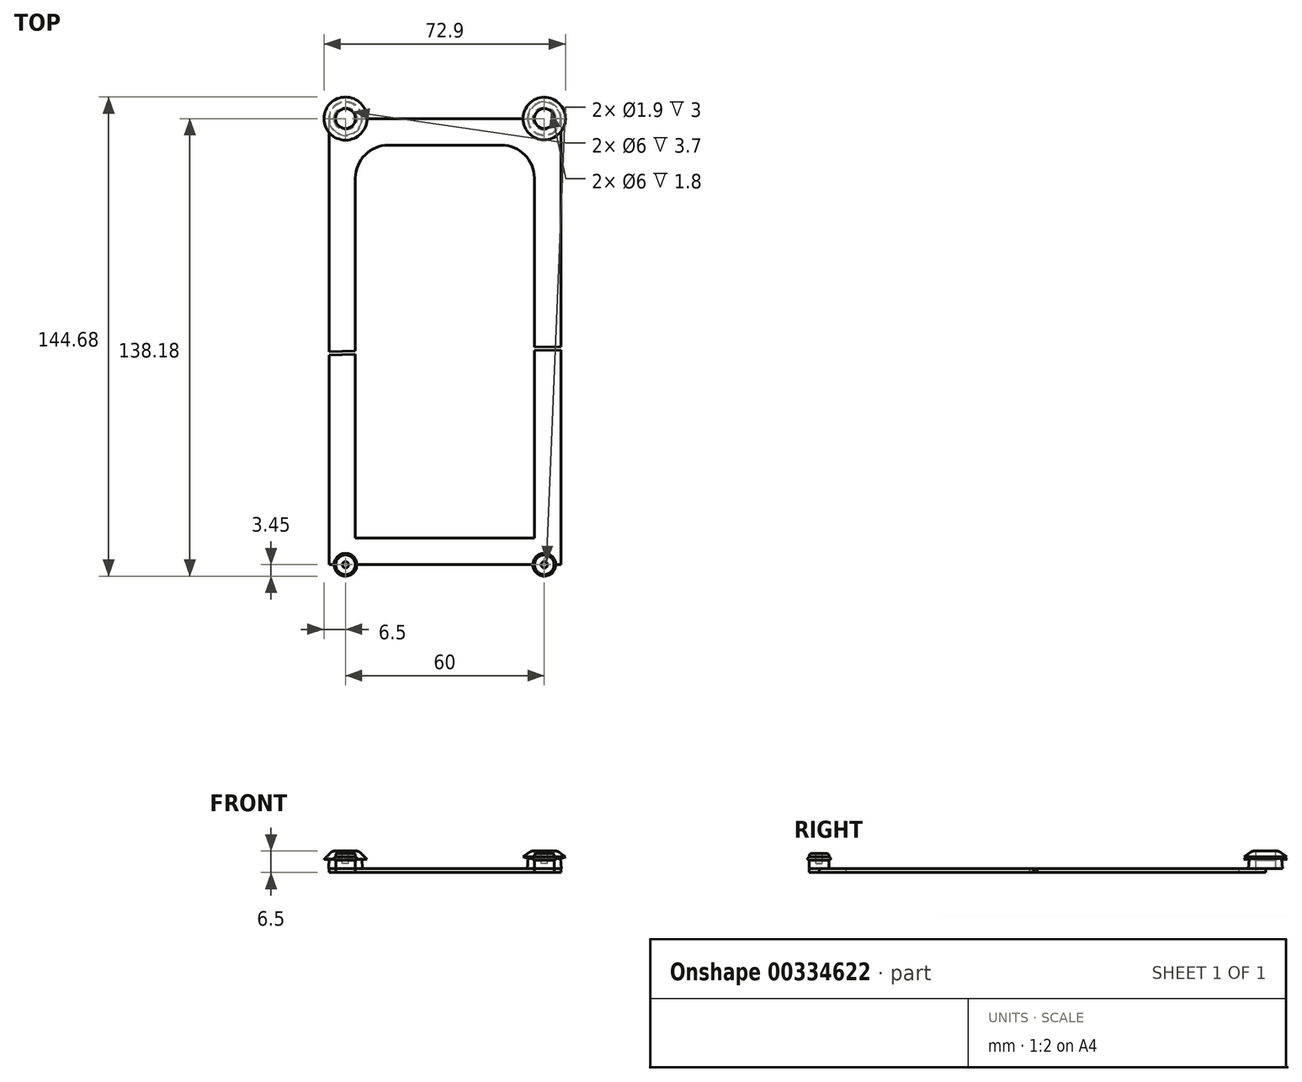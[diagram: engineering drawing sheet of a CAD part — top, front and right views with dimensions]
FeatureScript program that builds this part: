
annotation { "Feature Type Name" : "Feature", "Feature Type Description" : "" }
export const myFeature = defineFeature(function(context is Context, id is Id, definition is map)
    precondition{}
    {
        {
            var Q0;
            Q0=qCreatedBy(makeId("Front.planeOp"),FACE);
            var sketch = newSketch(context, id + "F0", { "sketchPlane" : qUnion([Q0])});
            skLineSegment(sketch, "E0", {"start": v(-3, 6.5) * mm, "end": v(-4, 6.5) * mm});
            skLineSegment(sketch, "E1", {"start": v(-4, 6.5) * mm, "end": v(-6.5, 4) * mm});
            skLineSegment(sketch, "E2", {"start": v(-6.5, 4) * mm, "end": v(-4.9, 4.4) * mm});
            skLineSegment(sketch, "E3", {"start": v(-3, 1.2) * mm, "end": v(-3, 3.7) * mm});
            skLineSegment(sketch, "E4", {"start": v(0, -15.71) * mm, "end": v(0, 21.33) * mm});
            skLineSegment(sketch, "E5", {"start": v(-5.1, 1.2) * mm, "end": v(-3, 1.2) * mm});
            skPoint(sketch, "E6.orphan", {"position": v(-3, 0) * mm});
            skLineSegment(sketch, "E7", {"start": v(-5.1, 1.2) * mm, "end": v(-4.9, 4.4) * mm});
            skArc(sketch, "E8", {"start": v(-3, 4.7) * mm, "mid": v(-3.5, 4.2) * mm, "end": v(-3, 3.7) * mm});
            skLineSegment(sketch, "E9.trimOffspring", {"start": v(-3, 4.7) * mm, "end": v(-3, 6.5) * mm});
            skSolve(sketch);
        }
        {
            var Q0;
            Q0 = qSketchRegion(id + "F0", true);
            var Q1;
            Q1=sQuery(id+"F0.wireOp",EDGE,"E4");
            revolve(context, id + "F1", {"entities" : qUnion([Q0]), "axis" : qUnion([Q1]), "revolveType" : RevolveType.FULL});
        }
        {
            var Q0;
            Q0=qCreatedBy(makeId("Front.planeOp"),FACE);
            var sketch = newSketch(context, id + "F2", { "sketchPlane" : qUnion([Q0])});
            skLineSegment(sketch, "E10", {"start": v(60, 20.21) * mm, "end": v(60, -31.14) * mm});
            skLineSegment(sketch, "E11", {"start": v(57, 1.2) * mm, "end": v(54.9, 1.2) * mm});
            skLineSegment(sketch, "E12", {"start": v(54.9, 1.2) * mm, "end": v(55.1, 4.2) * mm});
            skLineSegment(sketch, "E13", {"start": v(53.6, 4.7) * mm, "end": v(56, 6.5) * mm});
            skLineSegment(sketch, "E14", {"start": v(56, 6.5) * mm, "end": v(57, 6.5) * mm});
            skLineSegment(sketch, "E15", {"start": v(57, 6.5) * mm, "end": v(57, 4.7) * mm});
            skLineSegment(sketch, "E16", {"start": v(53.6, 4.7) * mm, "end": v(55.1, 4.2) * mm});
            skArc(sketch, "E17", {"start": v(57, 4.7) * mm, "mid": v(56.5, 4.2) * mm, "end": v(57, 3.7) * mm});
            skLineSegment(sketch, "E18.trimOffspring", {"start": v(57, 3.7) * mm, "end": v(57, 1.2) * mm});
            skLineSegment(sketch, "E19", {"start": v(60, 1.2) * mm, "end": v(60, 0) * mm});
            skLineSegment(sketch, "E20", {"start": v(60, 0) * mm, "end": v(60, 1.2) * mm});
            skSolve(sketch);
        }
        {
            var Q0;
            Q0=makeQuery(id+"F2.imprint","IMPRINT",FACE,{"disambiguationData":[TD([[makeQuery(id+"F2.imprint","IMPRINT",EDGE,{"derivedFrom":sQuery(id+"F2.wireOp",EDGE,"E11")}),-1.0]])]});
            var Q1;
            Q1=sQuery(id+"F2.wireOp",EDGE,"E10");
            revolve(context, id + "F3", {"surfaceOperationType" : NewSurfaceOperationType.NEW, "entities" : qUnion([Q0]), "axis" : qUnion([Q1]), "revolveType" : RevolveType.FULL});
        }
        {
            var Q0;
            Q0=qCreatedBy(makeId("Top.planeOp"),FACE);
            var sketch = newSketch(context, id + "F4", { "sketchPlane" : qUnion([Q0])});
            skLineSegment(sketch, "E21.left", {"start": v(-5, -8) * mm, "end": v(-5, -70.37) * mm});
            skArc(sketch, "E22", {"start": v(0, -3) * mm, "mid": v(2.12, -2.12) * mm, "end": v(3, 0) * mm});
            skArc(sketch, "E23", {"start": v(57, 0) * mm, "mid": v(57.88, -2.12) * mm, "end": v(60, -3) * mm});
            skCircle(sketch, "E24", {"center": v(60, -134.73) * mm, "radius": 2.95 * mm});
            skCircle(sketch, "E25", {"center": v(0, -134.73) * mm, "radius": 2.95 * mm});
            skLineSegment(sketch, "E26.bottom", {"start": v(3, -8) * mm, "end": v(57, -8) * mm});
            skLineSegment(sketch, "E26.top", {"start": v(3, -126.73) * mm, "end": v(57, -126.73) * mm});
            skLineSegment(sketch, "E26.left", {"start": v(3, -8) * mm, "end": v(3, -70.2) * mm});
            skLineSegment(sketch, "E26.right", {"start": v(57, -8) * mm, "end": v(57, -69.03) * mm});
            skLineSegment(sketch, "E27.bottom", {"start": v(2.95, -134.73) * mm, "end": v(57.05, -134.73) * mm});
            skLineSegment(sketch, "E28.bottom", {"start": v(3, 0) * mm, "end": v(57, 0) * mm});
            skLineSegment(sketch, "E29.right", {"start": v(65, -8) * mm, "end": v(65, -68.86) * mm});
            skPoint(sketch, "E30.orphan", {"position": v(70, -145.73) * mm});
            skArc(sketch, "E31", {"start": v(57, 0) * mm, "mid": v(60, -3) * mm, "end": v(63, 0) * mm});
            skArc(sketch, "E32", {"start": v(-3, 0) * mm, "mid": v(0, -3) * mm, "end": v(3, 0) * mm});
            skLineSegment(sketch, "E33.top", {"start": v(65, -134.73) * mm, "end": v(62.95, -134.73) * mm});
            skLineSegment(sketch, "E34.top", {"start": v(-5, -134.73) * mm, "end": v(-2.95, -134.73) * mm});
            skPoint(sketch, "E35.trimOffspring.start.orphan", {"position": v(60, -145.73) * mm});
            skPoint(sketch, "E36.orphan", {"position": v(65, -145.73) * mm});
            skLineSegment(sketch, "E37.top", {"start": v(65, 0) * mm, "end": v(63, 0) * mm});
            skLineSegment(sketch, "E37.left", {"start": v(65, -8) * mm, "end": v(65, 0) * mm});
            skLineSegment(sketch, "E38.top", {"start": v(-5, 0) * mm, "end": v(-3, 0) * mm});
            skLineSegment(sketch, "E38.left", {"start": v(-5, -8) * mm, "end": v(-5, 0) * mm});
            skPoint(sketch, "E39.orphan", {"position": v(0, 3) * mm});
            skLineSegment(sketch, "E40", {"start": v(-5, -71.37) * mm, "end": v(3, -71.2) * mm});
            skLineSegment(sketch, "E41", {"start": v(65, -68.86) * mm, "end": v(57, -69.03) * mm});
            skLineSegment(sketch, "E42.trimOffspring", {"start": v(65, -69.86) * mm, "end": v(65, -134.73) * mm});
            skLineSegment(sketch, "E43.trimOffspring", {"start": v(57, -70.03) * mm, "end": v(57, -126.73) * mm});
            skLineSegment(sketch, "E44.trimOffspring", {"start": v(3, -71.2) * mm, "end": v(3, -126.73) * mm});
            skLineSegment(sketch, "E45.trimOffspring", {"start": v(-5, -71.37) * mm, "end": v(-5, -134.73) * mm});
            skLineSegment(sketch, "E46.trimOffspring", {"start": v(57, -70.03) * mm, "end": v(65, -69.86) * mm});
            skLineSegment(sketch, "E47.trimOffspring", {"start": v(3, -70.2) * mm, "end": v(-5, -70.37) * mm});
            skSolve(sketch);
        }
        {
            var Q0;
            Q0 = qSketchRegion(id + "F4", true);
            extrude(context, id + "F5", {"entities" : qUnion([Q0]), "operationType" : NewBodyOperationType.ADD, "depth" : 1.2 * mm, "offsetDistance" : 25 * mm});
        }
        {
            var Q0;
            Q0=makeQuery(id+"F3.opRevolve","SWEPT_EDGE",EDGE,{"disambiguationData":[OSD([sQuery(id+"F2.wireOp",EDGE,"E13"),sQuery(id+"F2.wireOp",EDGE,"E14")])]});
            fillet(context, id + "F6", {"entities" : qUnion([Q0]), "radius" : 2 * mm, "tangentPropagation" : true, "allowEdgeOverflow" : false});
        }
        {
            var Q0;
            Q0=makeQuery(id+"F1.opRevolve","SWEPT_EDGE",EDGE,{"disambiguationData":[OSD([sQuery(id+"F0.wireOp",EDGE,"E0"),sQuery(id+"F0.wireOp",EDGE,"E1")])]});
            fillet(context, id + "F7", {"entities" : qUnion([Q0]), "radius" : 2 * mm, "tangentPropagation" : true, "allowEdgeOverflow" : false});
        }
        {
            var Q0;
            Q0=makeQuery(id+"F5.opExtrude","SWEPT_EDGE",EDGE,{"disambiguationData":[OSD([sQuery(id+"F4.wireOp",EDGE,"E26.bottom"),sQuery(id+"F4.wireOp",EDGE,"E26.left")])]});
            var Q1;
            Q1=makeQuery(id+"F5.opExtrude","SWEPT_EDGE",EDGE,{"disambiguationData":[OSD([sQuery(id+"F4.wireOp",EDGE,"E26.bottom"),sQuery(id+"F4.wireOp",EDGE,"E26.right")])]});
            fillet(context, id + "F8", {"entities" : qUnion([Q0, Q1]), "radius" : 10 * mm, "tangentPropagation" : true, "allowEdgeOverflow" : false});
        }
        {
            var Q0;
            Q0=qCreatedBy(makeId("Right.planeOp"),FACE);
            var sketch = newSketch(context, id + "F9", { "sketchPlane" : qUnion([Q0])});
            skLineSegment(sketch, "E48", {"start": v(-134.73, 15.66) * mm, "end": v(-134.73, -13.26) * mm});
            skLineSegment(sketch, "E49", {"start": v(-134.73, 1.2) * mm, "end": v(-137.68, 1.2) * mm});
            skLineSegment(sketch, "E50", {"start": v(-137.68, 1.2) * mm, "end": v(-137.68, 4.2) * mm});
            skLineSegment(sketch, "E51", {"start": v(-137.68, 5.7) * mm, "end": v(-135.68, 5.7) * mm});
            skLineSegment(sketch, "E52", {"start": v(-135.68, 5.7) * mm, "end": v(-135.68, 2.7) * mm});
            skLineSegment(sketch, "E53", {"start": v(-135.68, 2.7) * mm, "end": v(-134.73, 2.7) * mm});
            skLineSegment(sketch, "E54", {"start": v(-134.73, 2.7) * mm, "end": v(-134.73, 1.2) * mm});
            skArc(sketch, "E55", {"start": v(-137.68, 4.7) * mm, "mid": v(-138.18, 4.2) * mm, "end": v(-137.68, 3.7) * mm});
            skLineSegment(sketch, "E56.trimOffspring", {"start": v(-137.68, 4.7) * mm, "end": v(-137.68, 5.7) * mm});
            skLineSegment(sketch, "E57", {"start": v(-134.73, 1.2) * mm, "end": v(-134.73, 0) * mm});
            skSolve(sketch);
        }
        {
            var Q0;
            {var subQ1=sQuery(id+"F9.wireOp",EDGE,"E49");Q0=makeQuery(id+"F9.imprint","IMPRINT",FACE,{"disambiguationData":[TD([[makeQuery(id+"F9.imprint","IMPRINT",EDGE,{"derivedFrom":subQ1}),-1.0]])]});}
            var Q1;
            Q1=sQuery(id+"F9.wireOp",EDGE,"E48");
            revolve(context, id + "F10", {"surfaceOperationType" : NewSurfaceOperationType.NEW, "entities" : qUnion([Q0]), "axis" : qUnion([Q1]), "revolveType" : RevolveType.FULL});
        }
        {
            var Q0;
            Q0=makeQuery(id+"F10.opRevolve","SWEPT_EDGE",EDGE,{"disambiguationData":[OSD([sQuery(id+"F9.wireOp",EDGE,"E51"),sQuery(id+"F9.wireOp",EDGE,"E56.trimOffspring")])]});
            fillet(context, id + "F11", {"entities" : qUnion([Q0]), "radius" : 0.5 * mm, "tangentPropagation" : true, "allowEdgeOverflow" : false});
        }
        {
            var Q0;
            Q0=makeQuery(id+"F10.opRevolve","SWEPT_BODY",BODY,{"disambiguationData":[OSD([sQuery(id+"F9.wireOp",EDGE,"E49"),sQuery(id+"F9.wireOp",EDGE,"E50"),sQuery(id+"F9.wireOp",EDGE,"E51"),sQuery(id+"F9.wireOp",EDGE,"E52"),sQuery(id+"F9.wireOp",EDGE,"E53"),sQuery(id+"F9.wireOp",EDGE,"E54"),sQuery(id+"F9.wireOp",EDGE,"E55"),sQuery(id+"F9.wireOp",EDGE,"E56.trimOffspring")])]});
            transform(context, id + "F12", {"entities" : qUnion([Q0]), "transformType" : TransformType.TRANSLATION_3D, "dx" : 60 * mm, "dy" : 0 * mm, "dz" : 0 * mm, "makeCopy" : true});
        }
    });
